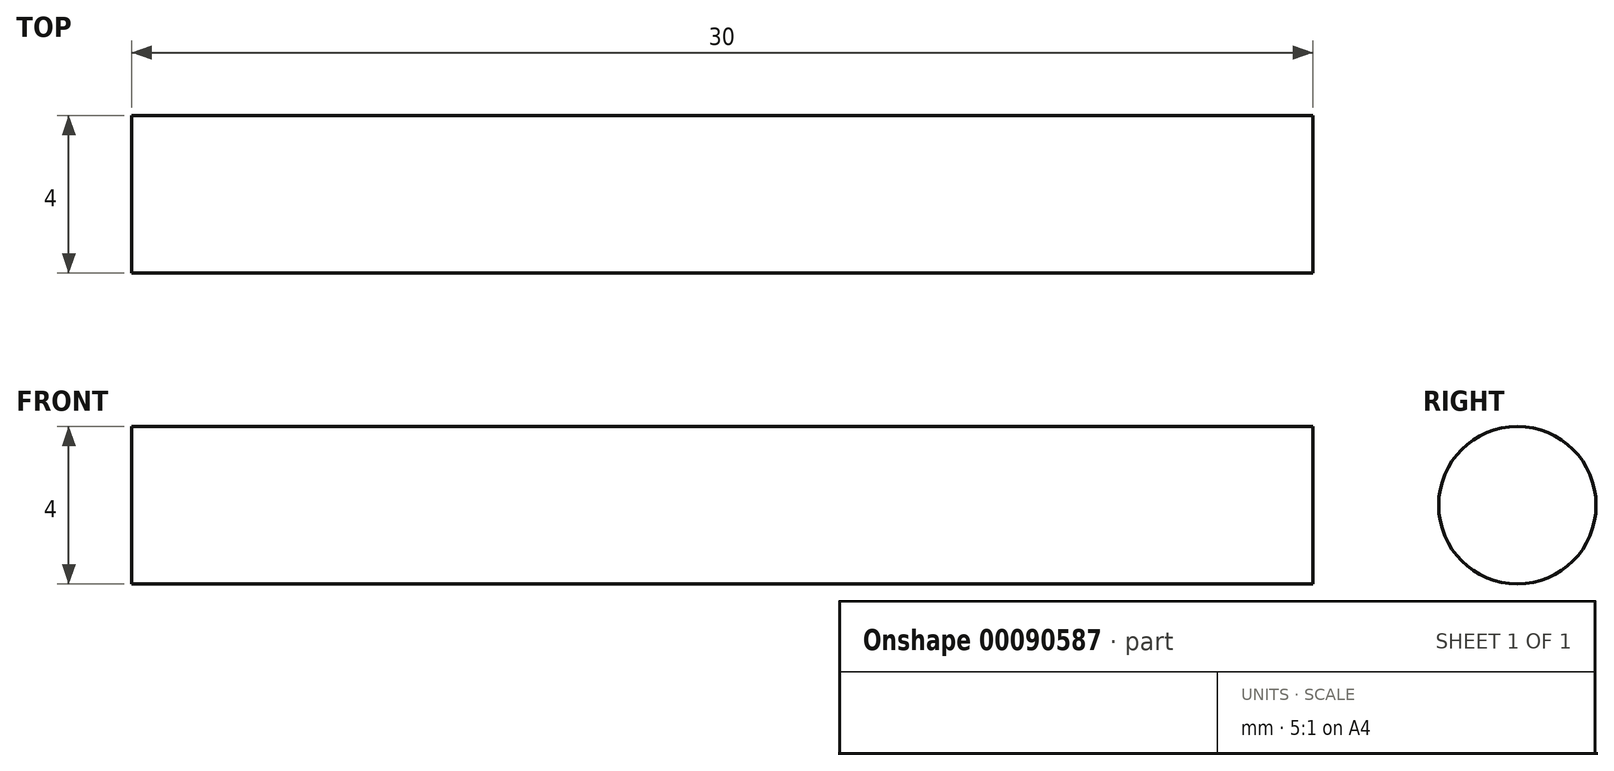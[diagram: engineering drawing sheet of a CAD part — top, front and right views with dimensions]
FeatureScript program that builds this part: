
annotation { "Feature Type Name" : "Feature", "Feature Type Description" : "" }
export const myFeature = defineFeature(function(context is Context, id is Id, definition is map)
    precondition{}
    {
        {
            var Q0;
            Q0=qCreatedBy(makeId("Right.planeOp"),FACE);
            var sketch = newSketch(context, id + "F0", { "sketchPlane" : qUnion([Q0])});
            skCircle(sketch, "E0", {"center": v(0, 0) * mm, "radius": 2 * mm});
            skSolve(sketch);
        }
        {
            var Q0;
            Q0=makeQuery(id+"F0.imprint","IMPRINT",FACE,{"disambiguationData":[TD([[makeQuery(id+"F0.imprint","IMPRINT",EDGE,{"derivedFrom":sQuery(id+"F0.wireOp",EDGE,"E0")}),1.0]])]});
            extrude(context, id + "F1", {"entities" : qUnion([Q0]), "depth" : 30 * mm});
        }
    });
